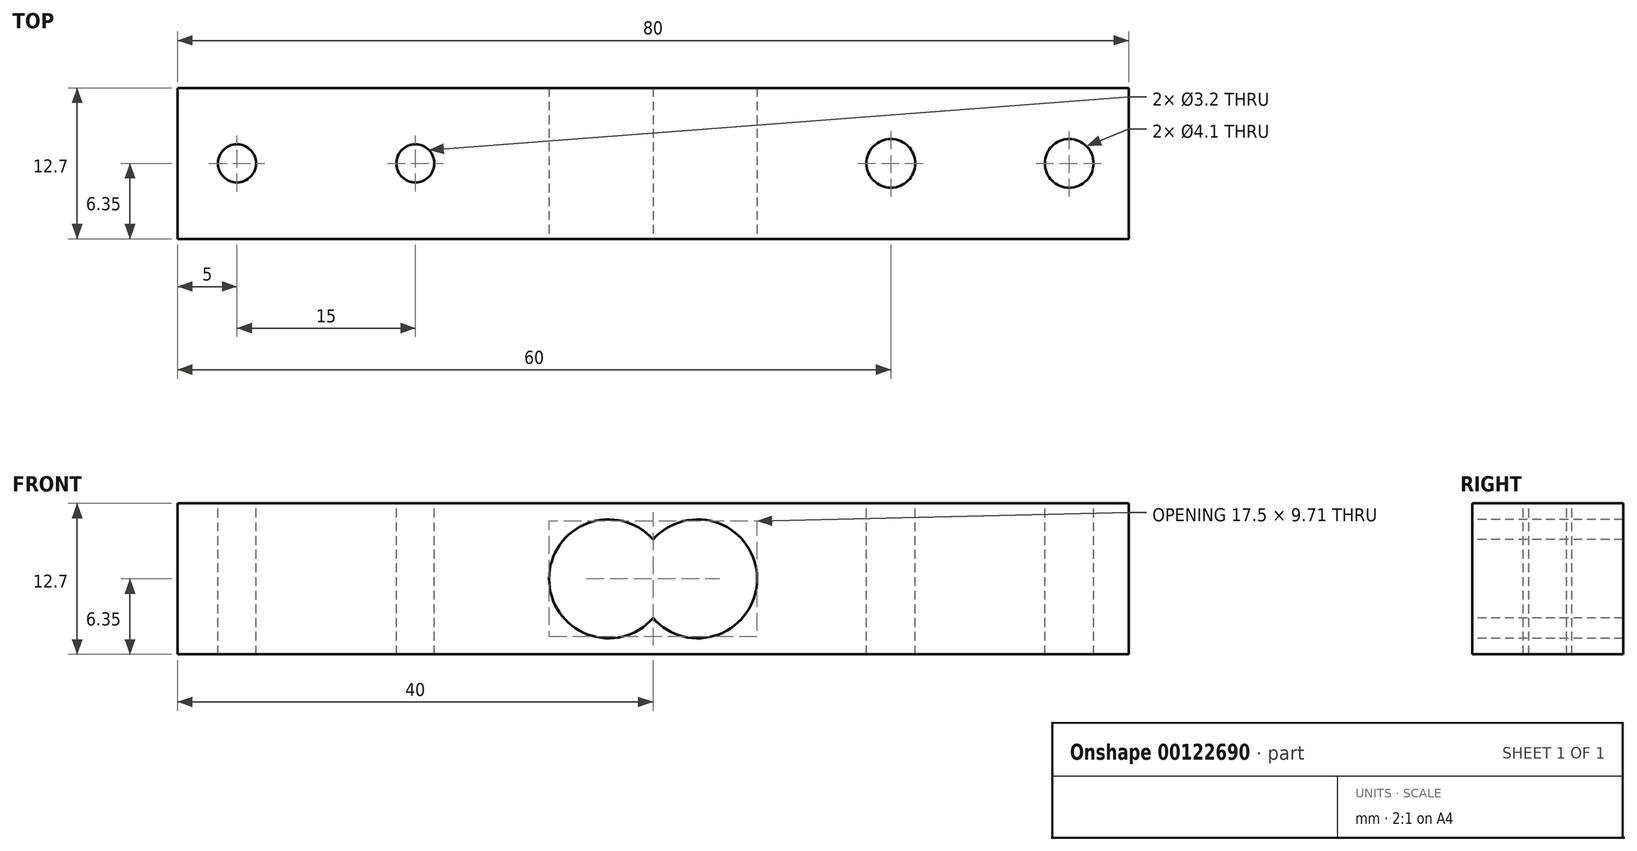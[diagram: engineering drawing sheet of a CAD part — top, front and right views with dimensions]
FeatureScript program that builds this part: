
annotation { "Feature Type Name" : "Feature", "Feature Type Description" : "" }
export const myFeature = defineFeature(function(context is Context, id is Id, definition is map)
    precondition{}
    {
        {
            var Q0;
            Q0=qCreatedBy(makeId("Top.planeOp"),FACE);
            var sketch = newSketch(context, id + "F0", { "sketchPlane" : qUnion([Q0])});
            skLineSegment(sketch, "E0.bottom", {"start": v(40, -6.35) * mm, "end": v(-40, -6.35) * mm});
            skLineSegment(sketch, "E0.top", {"start": v(40, 6.35) * mm, "end": v(-40, 6.35) * mm});
            skLineSegment(sketch, "E0.left", {"start": v(40, -6.35) * mm, "end": v(40, 6.35) * mm});
            skLineSegment(sketch, "E0.right", {"start": v(-40, -6.35) * mm, "end": v(-40, 6.35) * mm});
            skPoint(sketch, "E0.middle", {"position": v(0, 0) * mm});
            skSolve(sketch);
        }
        {
            var Q0;
            Q0 = qSketchRegion(id + "F0", true);
            extrude(context, id + "F1", {"entities" : qUnion([Q0]), "depth" : 12.7 * mm});
        }
        {
            var Q0;
            Q0=makeQuery(id+"F1.opExtrude","CAP_FACE",FACE,{"disambiguationData":[OSD([sQuery(id+"F0.wireOp",EDGE,"E0.bottom"),sQuery(id+"F0.wireOp",EDGE,"E0.top"),sQuery(id+"F0.wireOp",EDGE,"E0.left"),sQuery(id+"F0.wireOp",EDGE,"E0.right")])],"isStart":false});
            var sketch = newSketch(context, id + "F2", { "sketchPlane" : qUnion([Q0])});
            skPoint(sketch, "E1", {"position": v(-35, 0) * mm});
            skPoint(sketch, "E2", {"position": v(-20, 0) * mm});
            skPoint(sketch, "E3", {"position": v(20, 0) * mm});
            skPoint(sketch, "E4", {"position": v(35, 0) * mm});
            skSolve(sketch);
        }
        {
            var Q0;
            Q0=sQuery(id+"F2.wireOp",VERTEX,"E1");
            var Q1;
            Q1=sQuery(id+"F2.wireOp",VERTEX,"E2");
            var Q2;
            Q2=makeQuery(id+"F1.opExtrude","SWEPT_BODY",BODY,{"disambiguationData":[OSD([sQuery(id+"F0.wireOp",EDGE,"E0.bottom"),sQuery(id+"F0.wireOp",EDGE,"E0.top"),sQuery(id+"F0.wireOp",EDGE,"E0.left"),sQuery(id+"F0.wireOp",EDGE,"E0.right")])]});
            hole(context, id + "F3", {"style" : HoleStyle.SIMPLE, "endStyle" : HoleEndStyle.THROUGH, "standardTappedOrClearance" : lookupTablePath({ "standard" : "ISO", "engagement" : "75%", "pitch" : "0.75 mm", "size" : "M4", "type" : "Tapped" }), "standardBlindInLast" : lookupTablePath({ "standard" : "ISO", "engagement" : "75%", "pitch" : "0.75 mm", "size" : "M4", "type" : "Tapped" }), "holeDiameter" : 3.2 * mm, "locations" : qUnion([Q0, Q1]), "scope" : qUnion([Q2]), "isTappedThrough" : true, "showTappedDepth" : true});
        }
        {
            var Q0;
            Q0=makeQuery(id+"F1.opExtrude","CAP_FACE",FACE,{"disambiguationData":[OSD([sQuery(id+"F0.wireOp",EDGE,"E0.bottom"),sQuery(id+"F0.wireOp",EDGE,"E0.top"),sQuery(id+"F0.wireOp",EDGE,"E0.left"),sQuery(id+"F0.wireOp",EDGE,"E0.right")])],"isStart":false});
            var sketch = newSketch(context, id + "F4", { "sketchPlane" : qUnion([Q0])});
            skPoint(sketch, "E5", {"position": v(20, 0) * mm});
            skPoint(sketch, "E6", {"position": v(35, 0) * mm});
            skSolve(sketch);
        }
        {
            var Q0;
            Q0=sQuery(id+"F4.wireOp",VERTEX,"E5");
            var Q1;
            Q1=sQuery(id+"F4.wireOp",VERTEX,"E6");
            var Q2;
            Q2=makeQuery(id+"F1.opExtrude","SWEPT_BODY",BODY,{"disambiguationData":[OSD([sQuery(id+"F0.wireOp",EDGE,"E0.bottom"),sQuery(id+"F0.wireOp",EDGE,"E0.top"),sQuery(id+"F0.wireOp",EDGE,"E0.left"),sQuery(id+"F0.wireOp",EDGE,"E0.right")])]});
            hole(context, id + "F5", {"style" : HoleStyle.SIMPLE, "endStyle" : HoleEndStyle.THROUGH, "standardTappedOrClearance" : lookupTablePath({ "standard" : "ISO", "engagement" : "75%", "pitch" : "0.9 mm", "size" : "M5", "type" : "Tapped" }), "standardBlindInLast" : lookupTablePath({ "standard" : "ISO", "engagement" : "75%", "pitch" : "0.9 mm", "size" : "M5", "type" : "Tapped" }), "holeDiameter" : 4.1 * mm, "locations" : qUnion([Q0, Q1]), "scope" : qUnion([Q2]), "isTappedThrough" : true, "showTappedDepth" : true});
        }
        {
            var Q0;
            Q0=makeQuery(id+"F1.opExtrude","SWEPT_FACE",FACE,{"disambiguationData":[OSD([sQuery(id+"F0.wireOp",EDGE,"E0.bottom")])]});
            var sketch = newSketch(context, id + "F6", { "sketchPlane" : qUnion([Q0])});
            skPoint(sketch, "E7", {"position": v(-3.75, 6.35) * mm});
            skPoint(sketch, "E8", {"position": v(3.75, 6.35) * mm});
            skLineSegment(sketch, "E9", {"start": v(-3.75, 6.35) * mm, "end": v(3.75, 6.35) * mm});
            skLineSegment(sketch, "E10", {"start": v(-3.75, 0) * mm, "end": v(-3.75, 12.7) * mm});
            skSolve(sketch);
        }
        {
            var Q0;
            Q0=sQuery(id+"F6.wireOp",VERTEX,"E7");
            var Q1;
            Q1=sQuery(id+"F6.wireOp",VERTEX,"E8");
            var Q2;
            Q2=makeQuery(id+"F1.opExtrude","SWEPT_BODY",BODY,{"disambiguationData":[OSD([sQuery(id+"F0.wireOp",EDGE,"E0.bottom"),sQuery(id+"F0.wireOp",EDGE,"E0.top"),sQuery(id+"F0.wireOp",EDGE,"E0.left"),sQuery(id+"F0.wireOp",EDGE,"E0.right")])]});
            hole(context, id + "F7", {"style" : HoleStyle.SIMPLE, "endStyle" : HoleEndStyle.THROUGH, "holeDiameter" : 10 * mm, "locations" : qUnion([Q0, Q1]), "scope" : qUnion([Q2]), "isTappedThrough" : true});
        }
    });
